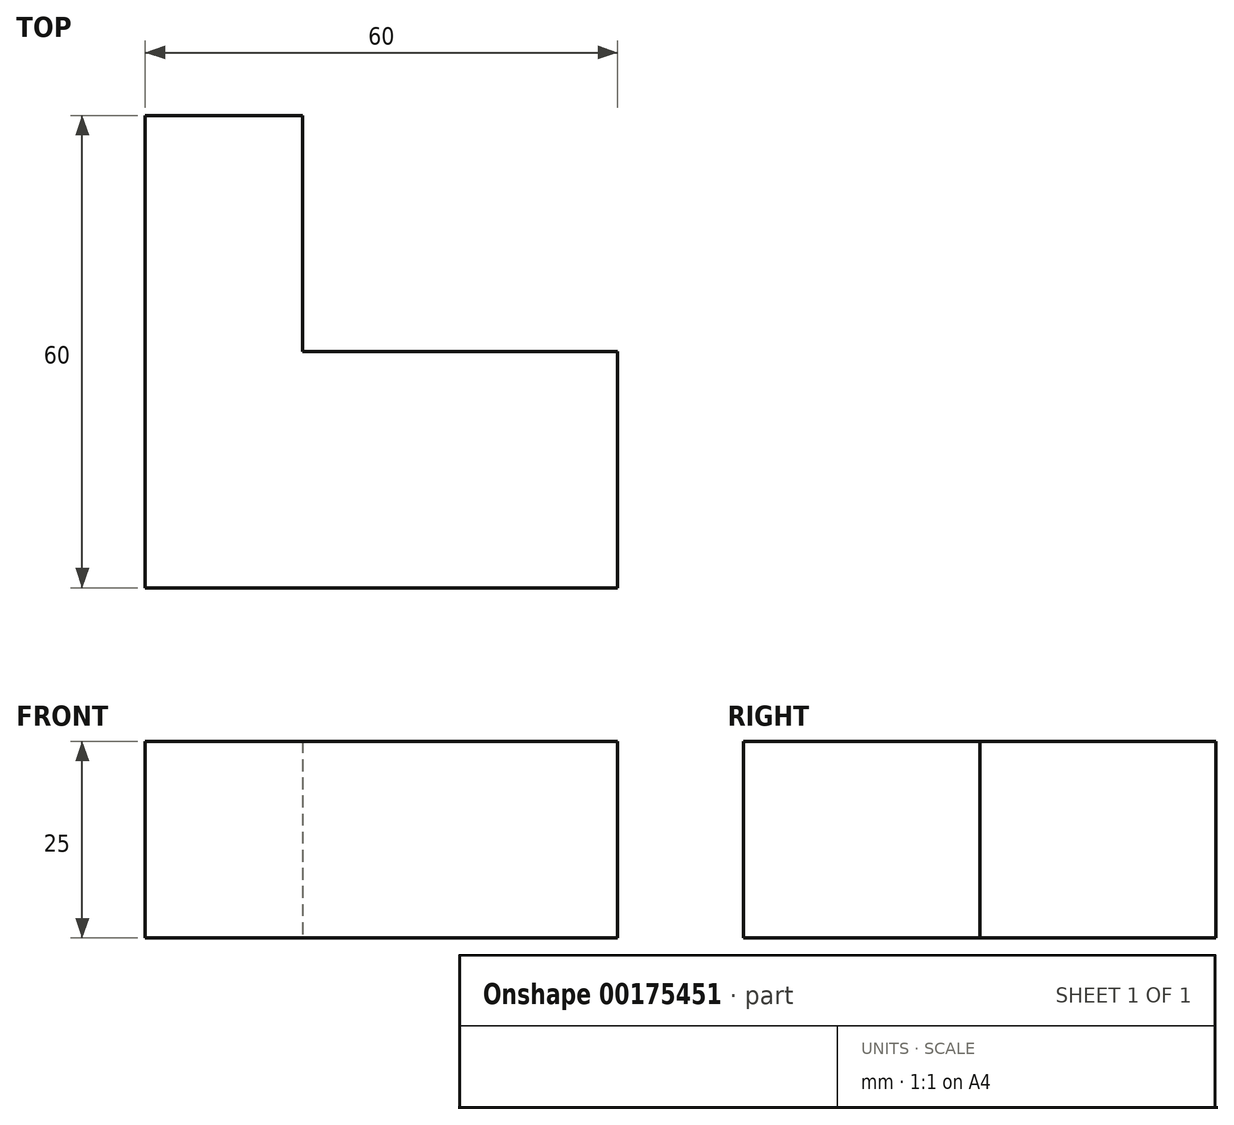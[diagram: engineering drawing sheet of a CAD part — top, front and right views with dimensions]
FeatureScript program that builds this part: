
annotation { "Feature Type Name" : "Feature", "Feature Type Description" : "" }
export const myFeature = defineFeature(function(context is Context, id is Id, definition is map)
    precondition{}
    {
        {
            var Q0;
            Q0=qCreatedBy(makeId("Top.planeOp"),FACE);
            var sketch = newSketch(context, id + "F0", { "sketchPlane" : qUnion([Q0])});
            skLineSegment(sketch, "E0", {"start": v(-43.91, 34.42) * mm, "end": v(-43.91, -25.58) * mm});
            skLineSegment(sketch, "E1", {"start": v(-43.91, 34.42) * mm, "end": v(-23.91, 34.42) * mm});
            skLineSegment(sketch, "E2", {"start": v(-43.91, -25.58) * mm, "end": v(16.09, -25.58) * mm});
            skLineSegment(sketch, "E3", {"start": v(16.09, -25.58) * mm, "end": v(16.09, 4.42) * mm});
            skLineSegment(sketch, "E4", {"start": v(-23.91, 34.42) * mm, "end": v(-23.91, 4.42) * mm});
            skLineSegment(sketch, "E5", {"start": v(-23.91, 4.42) * mm, "end": v(16.09, 4.42) * mm});
            skSolve(sketch);
        }
        {
            var Q0;
            Q0 = qSketchRegion(id + "F0", true);
            extrude(context, id + "F1", {"entities" : qUnion([Q0]), "depth" : 25 * mm});
        }
    });
